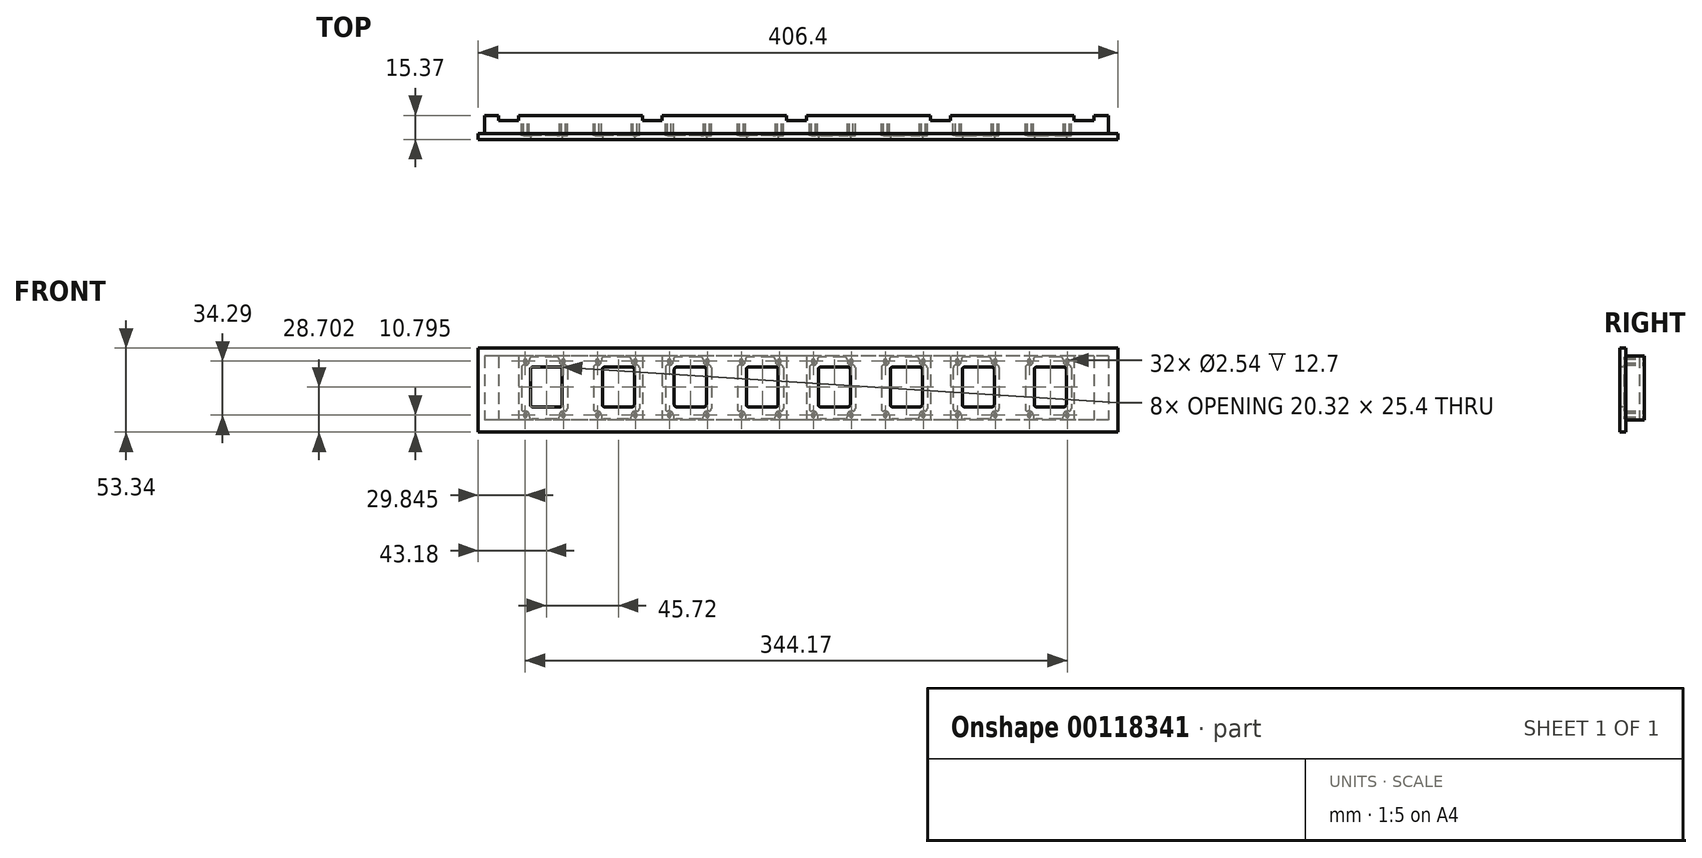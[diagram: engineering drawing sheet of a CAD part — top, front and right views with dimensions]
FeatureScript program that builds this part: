
annotation { "Feature Type Name" : "Feature", "Feature Type Description" : "" }
export const myFeature = defineFeature(function(context is Context, id is Id, definition is map)
    precondition{}
    {
        {
            var Q0;
            Q0=qCreatedBy(makeId("Front.planeOp"),FACE);
            var sketch = newSketch(context, id + "F0", { "sketchPlane" : qUnion([Q0])});
            skLineSegment(sketch, "E0.bottom", {"start": v(203.2, 26.67) * mm, "end": v(-203.2, 26.67) * mm});
            skLineSegment(sketch, "E0.top", {"start": v(203.2, -26.67) * mm, "end": v(-203.2, -26.67) * mm});
            skLineSegment(sketch, "E0.left", {"start": v(203.2, 26.67) * mm, "end": v(203.2, -26.67) * mm});
            skLineSegment(sketch, "E0.right", {"start": v(-203.2, 26.67) * mm, "end": v(-203.2, -26.67) * mm});
            skPoint(sketch, "E0.middle", {"position": v(0, 0) * mm});
            skSolve(sketch);
        }
        {
            var Q0;
            Q0 = qSketchRegion(id + "F0", true);
            extrude(context, id + "F1", {"entities" : qUnion([Q0]), "depth" : 3.8 * mm});
        }
        {
            var Q0;
            Q0=makeQuery(id+"F1.opExtrude","CAP_FACE",FACE,{"disambiguationData":[OSD([sQuery(id+"F0.wireOp",EDGE,"E0.bottom"),sQuery(id+"F0.wireOp",EDGE,"E0.top"),sQuery(id+"F0.wireOp",EDGE,"E0.left"),sQuery(id+"F0.wireOp",EDGE,"E0.right")])],"isStart":true});
            var sketch = newSketch(context, id + "F2", { "sketchPlane" : qUnion([Q0])});
            skLineSegment(sketch, "E1.bottom", {"start": v(-196.85, 21.59) * mm, "end": v(199.4, 21.59) * mm});
            skLineSegment(sketch, "E1.top", {"start": v(-196.85, -19.05) * mm, "end": v(199.4, -19.05) * mm});
            skLineSegment(sketch, "E1.left", {"start": v(-196.85, 21.59) * mm, "end": v(-196.85, -19.05) * mm});
            skLineSegment(sketch, "E1.right", {"start": v(199.4, 21.59) * mm, "end": v(199.4, -19.05) * mm});
            skSolve(sketch);
        }
        {
            var Q0;
            Q0 = qSketchRegion(id + "F2", true);
            extrude(context, id + "F3", {"entities" : qUnion([Q0]), "operationType" : NewBodyOperationType.ADD, "depth" : 11.56 * mm});
        }
        {
            var Q0;
            Q0=makeQuery(id+"F3.opExtrude","CAP_FACE",FACE,{"disambiguationData":[OSD([sQuery(id+"F2.wireOp",EDGE,"E1.bottom"),sQuery(id+"F2.wireOp",EDGE,"E1.top"),sQuery(id+"F2.wireOp",EDGE,"E1.left"),sQuery(id+"F2.wireOp",EDGE,"E1.right")])],"isStart":false});
            var sketch = newSketch(context, id + "F4", { "sketchPlane" : qUnion([Q0])});
            skLineSegment(sketch, "E2.bottom", {"start": v(-5.08, 21.59) * mm, "end": v(7.62, 21.59) * mm});
            skLineSegment(sketch, "E2.top", {"start": v(-5.08, -19.05) * mm, "end": v(7.62, -19.05) * mm});
            skLineSegment(sketch, "E2.left", {"start": v(-5.08, 21.59) * mm, "end": v(-5.08, -19.05) * mm});
            skLineSegment(sketch, "E2.right", {"start": v(7.62, 21.59) * mm, "end": v(7.62, -19.05) * mm});
            skLineSegment(sketch, "E3.1.0.0", {"start": v(86.36, -19.05) * mm, "end": v(99.06, -19.05) * mm});
            skLineSegment(sketch, "E3.1.0.1", {"start": v(86.36, 21.59) * mm, "end": v(99.06, 21.59) * mm});
            skLineSegment(sketch, "E3.1.0.2", {"start": v(86.36, 21.59) * mm, "end": v(86.36, -19.05) * mm});
            skLineSegment(sketch, "E3.1.0.3", {"start": v(99.06, 21.59) * mm, "end": v(99.06, -19.05) * mm});
            skLineSegment(sketch, "E3.2.0.0", {"start": v(177.8, -19.05) * mm, "end": v(190.5, -19.05) * mm});
            skLineSegment(sketch, "E3.2.0.1", {"start": v(177.8, 21.59) * mm, "end": v(190.5, 21.59) * mm});
            skLineSegment(sketch, "E3.2.0.2", {"start": v(177.8, 21.59) * mm, "end": v(177.8, -19.05) * mm});
            skLineSegment(sketch, "E3.2.0.3", {"start": v(190.5, 21.59) * mm, "end": v(190.5, -19.05) * mm});
            skLineSegment(sketch, "E3.direction1", {"start": v(-5.08, -19.05) * mm, "end": v(86.36, -19.05) * mm, "construction": true});
            skLineSegment(sketch, "E4.1.0.0", {"start": v(-96.52, 21.59) * mm, "end": v(-96.52, -19.05) * mm});
            skLineSegment(sketch, "E4.1.0.1", {"start": v(-96.52, -19.05) * mm, "end": v(-83.82, -19.05) * mm});
            skLineSegment(sketch, "E4.1.0.2", {"start": v(-96.52, 21.59) * mm, "end": v(-83.82, 21.59) * mm});
            skLineSegment(sketch, "E4.1.0.3", {"start": v(-83.82, 21.59) * mm, "end": v(-83.82, -19.05) * mm});
            skLineSegment(sketch, "E4.2.0.0", {"start": v(-187.96, 21.59) * mm, "end": v(-187.96, -19.05) * mm});
            skLineSegment(sketch, "E4.2.0.1", {"start": v(-187.96, -19.05) * mm, "end": v(-175.26, -19.05) * mm});
            skLineSegment(sketch, "E4.2.0.2", {"start": v(-187.96, 21.59) * mm, "end": v(-175.26, 21.59) * mm});
            skLineSegment(sketch, "E4.2.0.3", {"start": v(-175.26, 21.59) * mm, "end": v(-175.26, -19.05) * mm});
            skLineSegment(sketch, "E4.direction1", {"start": v(-5.08, -19.05) * mm, "end": v(-96.52, -19.05) * mm, "construction": true});
            skSolve(sketch);
        }
        {
            var Q0;
            Q0 = qSketchRegion(id + "F4", true);
            extrude(context, id + "F5", {"entities" : qUnion([Q0]), "operationType" : NewBodyOperationType.REMOVE, "oppositeDirection" : true, "depth" : 3.17 * mm});
        }
        {
            var Q0;
            {var subQ0=sQuery(id+"F2.wireOp",EDGE,"E1.bottom");var subQ1=sQuery(id+"F2.wireOp",EDGE,"E1.top");Q0=makeQuery(id+"F5.boolean.opBoolean","SPLIT",FACE,{"disambiguationData":[TD([makeQuery(id+"F5.opExtrude","SWEPT_FACE",FACE,{"disambiguationData":[OSD([sQuery(id+"F4.wireOp",EDGE,"E2.left")])]})])],"derivedFrom":makeQuery(id+"F3.opExtrude","CAP_FACE",FACE,{"disambiguationData":[OSD([subQ0,subQ1,sQuery(id+"F2.wireOp",EDGE,"E1.left"),sQuery(id+"F2.wireOp",EDGE,"E1.right")])],"isStart":false})});}
            var sketch = newSketch(context, id + "F6", { "sketchPlane" : qUnion([Q0])});
            skLineSegment(sketch, "E5.bottom", {"start": v(-174, 21.59) * mm, "end": v(-143.51, 21.59) * mm, "construction": true});
            skLineSegment(sketch, "E5.top", {"start": v(-174, -19.05) * mm, "end": v(-143.51, -19.05) * mm, "construction": true});
            skLineSegment(sketch, "E5.left", {"start": v(-174, 21.59) * mm, "end": v(-174, -19.05) * mm, "construction": true});
            skLineSegment(sketch, "E5.right", {"start": v(-143.51, 21.59) * mm, "end": v(-143.51, -19.05) * mm, "construction": true});
            skCircle(sketch, "E6", {"center": v(-170.82, 18.41) * mm, "radius": 1.27 * mm});
            skCircle(sketch, "E7", {"center": v(-146.69, 18.41) * mm, "radius": 1.27 * mm});
            skCircle(sketch, "E8", {"center": v(-146.69, -15.88) * mm, "radius": 1.27 * mm});
            skCircle(sketch, "E9", {"center": v(-170.82, -15.88) * mm, "radius": 1.27 * mm});
            skArc(sketch, "E10", {"start": v(-170.82, 15.87) * mm, "mid": v(-169.02, 16.62) * mm, "end": v(-168.28, 18.41) * mm});
            skArc(sketch, "E11", {"start": v(-149.23, 18.41) * mm, "mid": v(-148.48, 16.62) * mm, "end": v(-146.69, 15.87) * mm});
            skArc(sketch, "E12", {"start": v(-168.28, -15.88) * mm, "mid": v(-169.02, -14.08) * mm, "end": v(-170.82, -13.34) * mm});
            skArc(sketch, "E13", {"start": v(-146.69, -13.34) * mm, "mid": v(-148.48, -14.08) * mm, "end": v(-149.23, -15.88) * mm});
            skLineSegment(sketch, "E14.top", {"start": v(-168.28, -18.42) * mm, "end": v(-149.23, -18.42) * mm});
            skLineSegment(sketch, "E14.left", {"start": v(-173.36, 15.87) * mm, "end": v(-173.36, -13.34) * mm});
            skLineSegment(sketch, "E14.right", {"start": v(-144.15, 15.87) * mm, "end": v(-144.15, -13.33) * mm});
            skLineSegment(sketch, "E15", {"start": v(-173.36, 15.87) * mm, "end": v(-170.82, 15.87) * mm});
            skLineSegment(sketch, "E16", {"start": v(-173.36, -13.34) * mm, "end": v(-170.82, -13.34) * mm});
            skLineSegment(sketch, "E17", {"start": v(-168.28, 20.95) * mm, "end": v(-168.28, 18.41) * mm});
            skLineSegment(sketch, "E18", {"start": v(-149.23, 20.95) * mm, "end": v(-149.23, 18.41) * mm});
            skLineSegment(sketch, "E19.trimOffspring", {"start": v(-168.28, 20.95) * mm, "end": v(-149.23, 20.95) * mm});
            skLineSegment(sketch, "E20.trimOffspring", {"start": v(-168.28, -15.88) * mm, "end": v(-168.28, -18.42) * mm});
            skLineSegment(sketch, "E21.trimOffspring", {"start": v(-146.69, 15.87) * mm, "end": v(-144.15, 15.87) * mm});
            skLineSegment(sketch, "E22.trimOffspring", {"start": v(-149.23, -15.88) * mm, "end": v(-149.23, -18.42) * mm});
            skLineSegment(sketch, "E23.trimOffspring", {"start": v(-146.69, -13.33) * mm, "end": v(-144.15, -13.33) * mm});
            skLineSegment(sketch, "E24.bottom", {"start": v(-169.17, 14.6) * mm, "end": v(-148.85, 14.6) * mm, "construction": true});
            skLineSegment(sketch, "E24.top", {"start": v(-169.17, -13.33) * mm, "end": v(-148.85, -13.33) * mm, "construction": true});
            skLineSegment(sketch, "E24.left", {"start": v(-169.17, 14.6) * mm, "end": v(-169.17, -13.33) * mm, "construction": true});
            skLineSegment(sketch, "E24.right", {"start": v(-148.85, 14.6) * mm, "end": v(-148.85, -13.33) * mm, "construction": true});
            skLineSegment(sketch, "E25.1.0.0", {"start": v(-128.27, -19.05) * mm, "end": v(-97.8, -19.05) * mm, "construction": true});
            skLineSegment(sketch, "E25.1.0.1", {"start": v(-97.8, 21.59) * mm, "end": v(-97.8, -19.05) * mm, "construction": true});
            skLineSegment(sketch, "E25.1.0.2", {"start": v(-128.27, 21.59) * mm, "end": v(-128.27, -19.05) * mm, "construction": true});
            skLineSegment(sketch, "E25.1.0.3", {"start": v(-123.45, 14.6) * mm, "end": v(-123.45, -13.33) * mm, "construction": true});
            skLineSegment(sketch, "E25.1.0.4", {"start": v(-103.13, 14.6) * mm, "end": v(-103.13, -13.33) * mm, "construction": true});
            skLineSegment(sketch, "E25.1.0.5", {"start": v(-123.45, -13.33) * mm, "end": v(-103.13, -13.33) * mm, "construction": true});
            skLineSegment(sketch, "E25.1.0.6", {"start": v(-123.45, 14.6) * mm, "end": v(-103.13, 14.6) * mm, "construction": true});
            skLineSegment(sketch, "E25.1.0.7", {"start": v(-128.27, 21.59) * mm, "end": v(-97.8, 21.59) * mm, "construction": true});
            skLineSegment(sketch, "E25.1.0.8", {"start": v(-98.43, 15.87) * mm, "end": v(-98.43, -13.33) * mm});
            skLineSegment(sketch, "E25.1.0.9", {"start": v(-122.56, 20.95) * mm, "end": v(-103.5, 20.95) * mm});
            skLineSegment(sketch, "E25.1.0.10", {"start": v(-122.55, -18.42) * mm, "end": v(-103.5, -18.42) * mm});
            skLineSegment(sketch, "E25.1.0.11", {"start": v(-127.64, 15.87) * mm, "end": v(-127.64, -13.34) * mm});
            skCircle(sketch, "E25.1.0.12", {"center": v(-125.1, 18.41) * mm, "radius": 1.27 * mm});
            skCircle(sketch, "E25.1.0.13", {"center": v(-125.1, -15.88) * mm, "radius": 1.27 * mm});
            skLineSegment(sketch, "E25.1.0.14", {"start": v(-122.55, -15.88) * mm, "end": v(-122.55, -18.42) * mm});
            skLineSegment(sketch, "E25.1.0.15", {"start": v(-122.55, 20.95) * mm, "end": v(-122.55, 18.41) * mm});
            skCircle(sketch, "E25.1.0.16", {"center": v(-100.97, 18.41) * mm, "radius": 1.27 * mm});
            skLineSegment(sketch, "E25.1.0.17", {"start": v(-127.64, -13.33) * mm, "end": v(-125.1, -13.33) * mm});
            skLineSegment(sketch, "E25.1.0.18", {"start": v(-103.5, 20.95) * mm, "end": v(-103.5, 18.41) * mm});
            skArc(sketch, "E25.1.0.19", {"start": v(-122.56, -15.88) * mm, "mid": v(-123.3, -14.08) * mm, "end": v(-125.1, -13.34) * mm});
            skArc(sketch, "E25.1.0.20", {"start": v(-103.5, 18.41) * mm, "mid": v(-102.76, 16.62) * mm, "end": v(-100.97, 15.87) * mm});
            skArc(sketch, "E25.1.0.21", {"start": v(-125.1, 15.87) * mm, "mid": v(-123.3, 16.62) * mm, "end": v(-122.56, 18.41) * mm});
            skLineSegment(sketch, "E25.1.0.22", {"start": v(-103.5, -15.88) * mm, "end": v(-103.5, -18.42) * mm});
            skLineSegment(sketch, "E25.1.0.23", {"start": v(-127.64, 15.88) * mm, "end": v(-125.1, 15.88) * mm});
            skCircle(sketch, "E25.1.0.24", {"center": v(-100.97, -15.88) * mm, "radius": 1.27 * mm});
            skLineSegment(sketch, "E25.1.0.25", {"start": v(-100.97, 15.87) * mm, "end": v(-98.43, 15.87) * mm});
            skArc(sketch, "E25.1.0.26", {"start": v(-100.97, -13.34) * mm, "mid": v(-102.76, -14.08) * mm, "end": v(-103.5, -15.88) * mm});
            skLineSegment(sketch, "E25.1.0.27", {"start": v(-100.97, -13.33) * mm, "end": v(-98.43, -13.33) * mm});
            skLineSegment(sketch, "E25.2.0.0", {"start": v(-82.55, -19.05) * mm, "end": v(-52.07, -19.05) * mm, "construction": true});
            skLineSegment(sketch, "E25.2.0.1", {"start": v(-52.07, 21.59) * mm, "end": v(-52.07, -19.05) * mm, "construction": true});
            skLineSegment(sketch, "E25.2.0.2", {"start": v(-82.55, 21.59) * mm, "end": v(-82.55, -19.05) * mm, "construction": true});
            skLineSegment(sketch, "E25.2.0.3", {"start": v(-77.73, 14.6) * mm, "end": v(-77.73, -13.33) * mm, "construction": true});
            skLineSegment(sketch, "E25.2.0.4", {"start": v(-57.41, 14.6) * mm, "end": v(-57.41, -13.33) * mm, "construction": true});
            skLineSegment(sketch, "E25.2.0.5", {"start": v(-77.73, -13.33) * mm, "end": v(-57.41, -13.33) * mm, "construction": true});
            skLineSegment(sketch, "E25.2.0.6", {"start": v(-77.73, 14.6) * mm, "end": v(-57.41, 14.6) * mm, "construction": true});
            skLineSegment(sketch, "E25.2.0.7", {"start": v(-82.55, 21.59) * mm, "end": v(-52.07, 21.59) * mm, "construction": true});
            skLineSegment(sketch, "E25.2.0.8", {"start": v(-52.7, 15.87) * mm, "end": v(-52.7, -13.33) * mm});
            skLineSegment(sketch, "E25.2.0.9", {"start": v(-76.84, 20.95) * mm, "end": v(-57.79, 20.95) * mm});
            skLineSegment(sketch, "E25.2.0.10", {"start": v(-76.83, -18.42) * mm, "end": v(-57.79, -18.42) * mm});
            skLineSegment(sketch, "E25.2.0.11", {"start": v(-81.91, 15.87) * mm, "end": v(-81.91, -13.34) * mm});
            skCircle(sketch, "E25.2.0.12", {"center": v(-79.38, 18.41) * mm, "radius": 1.27 * mm});
            skCircle(sketch, "E25.2.0.13", {"center": v(-79.38, -15.88) * mm, "radius": 1.27 * mm});
            skLineSegment(sketch, "E25.2.0.14", {"start": v(-76.83, -15.88) * mm, "end": v(-76.83, -18.42) * mm});
            skLineSegment(sketch, "E25.2.0.15", {"start": v(-76.83, 20.95) * mm, "end": v(-76.83, 18.41) * mm});
            skCircle(sketch, "E25.2.0.16", {"center": v(-55.25, 18.41) * mm, "radius": 1.27 * mm});
            skLineSegment(sketch, "E25.2.0.17", {"start": v(-81.91, -13.33) * mm, "end": v(-79.38, -13.33) * mm});
            skLineSegment(sketch, "E25.2.0.18", {"start": v(-57.79, 20.95) * mm, "end": v(-57.79, 18.41) * mm});
            skArc(sketch, "E25.2.0.19", {"start": v(-76.83, -15.88) * mm, "mid": v(-77.58, -14.08) * mm, "end": v(-79.38, -13.34) * mm});
            skArc(sketch, "E25.2.0.20", {"start": v(-57.79, 18.41) * mm, "mid": v(-57.04, 16.62) * mm, "end": v(-55.25, 15.87) * mm});
            skArc(sketch, "E25.2.0.21", {"start": v(-79.38, 15.87) * mm, "mid": v(-77.58, 16.62) * mm, "end": v(-76.83, 18.41) * mm});
            skLineSegment(sketch, "E25.2.0.22", {"start": v(-57.79, -15.88) * mm, "end": v(-57.79, -18.42) * mm});
            skLineSegment(sketch, "E25.2.0.23", {"start": v(-81.91, 15.88) * mm, "end": v(-79.38, 15.88) * mm});
            skCircle(sketch, "E25.2.0.24", {"center": v(-55.25, -15.88) * mm, "radius": 1.27 * mm});
            skLineSegment(sketch, "E25.2.0.25", {"start": v(-55.25, 15.87) * mm, "end": v(-52.7, 15.87) * mm});
            skArc(sketch, "E25.2.0.26", {"start": v(-55.25, -13.34) * mm, "mid": v(-57.04, -14.08) * mm, "end": v(-57.79, -15.88) * mm});
            skLineSegment(sketch, "E25.2.0.27", {"start": v(-55.25, -13.33) * mm, "end": v(-52.7, -13.33) * mm});
            skLineSegment(sketch, "E25.3.0.0", {"start": v(-36.83, -19.05) * mm, "end": v(-6.35, -19.05) * mm, "construction": true});
            skLineSegment(sketch, "E25.3.0.1", {"start": v(-6.35, 21.59) * mm, "end": v(-6.35, -19.05) * mm, "construction": true});
            skLineSegment(sketch, "E25.3.0.2", {"start": v(-36.83, 21.59) * mm, "end": v(-36.83, -19.05) * mm, "construction": true});
            skLineSegment(sketch, "E25.3.0.3", {"start": v(-32.01, 14.6) * mm, "end": v(-32.01, -13.33) * mm, "construction": true});
            skLineSegment(sketch, "E25.3.0.4", {"start": v(-11.7, 14.6) * mm, "end": v(-11.7, -13.33) * mm, "construction": true});
            skLineSegment(sketch, "E25.3.0.5", {"start": v(-32.01, -13.33) * mm, "end": v(-11.7, -13.33) * mm, "construction": true});
            skLineSegment(sketch, "E25.3.0.6", {"start": v(-32.01, 14.6) * mm, "end": v(-11.7, 14.6) * mm, "construction": true});
            skLineSegment(sketch, "E25.3.0.7", {"start": v(-36.83, 21.59) * mm, "end": v(-6.35, 21.59) * mm, "construction": true});
            skLineSegment(sketch, "E25.3.0.8", {"start": v(-6.98, 15.87) * mm, "end": v(-6.98, -13.33) * mm});
            skLineSegment(sketch, "E25.3.0.9", {"start": v(-31.12, 20.95) * mm, "end": v(-12.07, 20.95) * mm});
            skLineSegment(sketch, "E25.3.0.10", {"start": v(-31.11, -18.42) * mm, "end": v(-12.07, -18.42) * mm});
            skLineSegment(sketch, "E25.3.0.11", {"start": v(-36.2, 15.87) * mm, "end": v(-36.2, -13.34) * mm});
            skCircle(sketch, "E25.3.0.12", {"center": v(-33.65, 18.41) * mm, "radius": 1.27 * mm});
            skCircle(sketch, "E25.3.0.13", {"center": v(-33.65, -15.88) * mm, "radius": 1.27 * mm});
            skLineSegment(sketch, "E25.3.0.14", {"start": v(-31.11, -15.88) * mm, "end": v(-31.11, -18.42) * mm});
            skLineSegment(sketch, "E25.3.0.15", {"start": v(-31.11, 20.95) * mm, "end": v(-31.11, 18.41) * mm});
            skCircle(sketch, "E25.3.0.16", {"center": v(-9.53, 18.41) * mm, "radius": 1.27 * mm});
            skLineSegment(sketch, "E25.3.0.17", {"start": v(-36.2, -13.33) * mm, "end": v(-33.65, -13.33) * mm});
            skLineSegment(sketch, "E25.3.0.18", {"start": v(-12.07, 20.95) * mm, "end": v(-12.07, 18.41) * mm});
            skArc(sketch, "E25.3.0.19", {"start": v(-31.11, -15.88) * mm, "mid": v(-31.86, -14.08) * mm, "end": v(-33.65, -13.34) * mm});
            skArc(sketch, "E25.3.0.20", {"start": v(-12.07, 18.41) * mm, "mid": v(-11.32, 16.62) * mm, "end": v(-9.53, 15.87) * mm});
            skArc(sketch, "E25.3.0.21", {"start": v(-33.65, 15.87) * mm, "mid": v(-31.86, 16.62) * mm, "end": v(-31.11, 18.41) * mm});
            skLineSegment(sketch, "E25.3.0.22", {"start": v(-12.07, -15.88) * mm, "end": v(-12.07, -18.42) * mm});
            skLineSegment(sketch, "E25.3.0.23", {"start": v(-36.2, 15.88) * mm, "end": v(-33.65, 15.88) * mm});
            skCircle(sketch, "E25.3.0.24", {"center": v(-9.53, -15.88) * mm, "radius": 1.27 * mm});
            skLineSegment(sketch, "E25.3.0.25", {"start": v(-9.53, 15.87) * mm, "end": v(-6.98, 15.87) * mm});
            skArc(sketch, "E25.3.0.26", {"start": v(-9.53, -13.34) * mm, "mid": v(-11.32, -14.08) * mm, "end": v(-12.07, -15.88) * mm});
            skLineSegment(sketch, "E25.3.0.27", {"start": v(-9.53, -13.33) * mm, "end": v(-6.98, -13.33) * mm});
            skLineSegment(sketch, "E25.4.0.0", {"start": v(8.9, -19.05) * mm, "end": v(39.37, -19.05) * mm, "construction": true});
            skLineSegment(sketch, "E25.4.0.1", {"start": v(39.37, 21.59) * mm, "end": v(39.37, -19.05) * mm, "construction": true});
            skLineSegment(sketch, "E25.4.0.2", {"start": v(8.9, 21.59) * mm, "end": v(8.9, -19.05) * mm, "construction": true});
            skLineSegment(sketch, "E25.4.0.3", {"start": v(13.7, 14.6) * mm, "end": v(13.7, -13.33) * mm, "construction": true});
            skLineSegment(sketch, "E25.4.0.4", {"start": v(34.03, 14.6) * mm, "end": v(34.03, -13.33) * mm, "construction": true});
            skLineSegment(sketch, "E25.4.0.5", {"start": v(13.7, -13.33) * mm, "end": v(34.03, -13.33) * mm, "construction": true});
            skLineSegment(sketch, "E25.4.0.6", {"start": v(13.7, 14.6) * mm, "end": v(34.03, 14.6) * mm, "construction": true});
            skLineSegment(sketch, "E25.4.0.7", {"start": v(8.9, 21.59) * mm, "end": v(39.37, 21.59) * mm, "construction": true});
            skLineSegment(sketch, "E25.4.0.8", {"start": v(38.74, 15.87) * mm, "end": v(38.74, -13.33) * mm});
            skLineSegment(sketch, "E25.4.0.9", {"start": v(14.6, 20.95) * mm, "end": v(33.65, 20.95) * mm});
            skLineSegment(sketch, "E25.4.0.10", {"start": v(14.6, -18.42) * mm, "end": v(33.65, -18.42) * mm});
            skLineSegment(sketch, "E25.4.0.11", {"start": v(9.53, 15.87) * mm, "end": v(9.53, -13.34) * mm});
            skCircle(sketch, "E25.4.0.12", {"center": v(12.07, 18.41) * mm, "radius": 1.27 * mm});
            skCircle(sketch, "E25.4.0.13", {"center": v(12.07, -15.88) * mm, "radius": 1.27 * mm});
            skLineSegment(sketch, "E25.4.0.14", {"start": v(14.6, -15.88) * mm, "end": v(14.6, -18.42) * mm});
            skLineSegment(sketch, "E25.4.0.15", {"start": v(14.6, 20.95) * mm, "end": v(14.6, 18.41) * mm});
            skCircle(sketch, "E25.4.0.16", {"center": v(36.2, 18.41) * mm, "radius": 1.27 * mm});
            skLineSegment(sketch, "E25.4.0.17", {"start": v(9.53, -13.33) * mm, "end": v(12.07, -13.33) * mm});
            skLineSegment(sketch, "E25.4.0.18", {"start": v(33.65, 20.95) * mm, "end": v(33.65, 18.41) * mm});
            skArc(sketch, "E25.4.0.19", {"start": v(14.6, -15.88) * mm, "mid": v(13.86, -14.08) * mm, "end": v(12.07, -13.34) * mm});
            skArc(sketch, "E25.4.0.20", {"start": v(33.66, 18.41) * mm, "mid": v(34.4, 16.62) * mm, "end": v(36.2, 15.87) * mm});
            skArc(sketch, "E25.4.0.21", {"start": v(12.07, 15.87) * mm, "mid": v(13.86, 16.62) * mm, "end": v(14.6, 18.41) * mm});
            skLineSegment(sketch, "E25.4.0.22", {"start": v(33.65, -15.88) * mm, "end": v(33.65, -18.42) * mm});
            skLineSegment(sketch, "E25.4.0.23", {"start": v(9.53, 15.88) * mm, "end": v(12.07, 15.88) * mm});
            skCircle(sketch, "E25.4.0.24", {"center": v(36.2, -15.88) * mm, "radius": 1.27 * mm});
            skLineSegment(sketch, "E25.4.0.25", {"start": v(36.2, 15.87) * mm, "end": v(38.74, 15.87) * mm});
            skArc(sketch, "E25.4.0.26", {"start": v(36.2, -13.34) * mm, "mid": v(34.4, -14.08) * mm, "end": v(33.66, -15.88) * mm});
            skLineSegment(sketch, "E25.4.0.27", {"start": v(36.2, -13.33) * mm, "end": v(38.74, -13.33) * mm});
            skLineSegment(sketch, "E25.5.0.0", {"start": v(54.61, -19.05) * mm, "end": v(85.1, -19.05) * mm, "construction": true});
            skLineSegment(sketch, "E25.5.0.1", {"start": v(85.1, 21.59) * mm, "end": v(85.1, -19.05) * mm, "construction": true});
            skLineSegment(sketch, "E25.5.0.2", {"start": v(54.61, 21.59) * mm, "end": v(54.61, -19.05) * mm, "construction": true});
            skLineSegment(sketch, "E25.5.0.3", {"start": v(59.43, 14.6) * mm, "end": v(59.43, -13.33) * mm, "construction": true});
            skLineSegment(sketch, "E25.5.0.4", {"start": v(79.75, 14.6) * mm, "end": v(79.75, -13.33) * mm, "construction": true});
            skLineSegment(sketch, "E25.5.0.5", {"start": v(59.43, -13.33) * mm, "end": v(79.75, -13.33) * mm, "construction": true});
            skLineSegment(sketch, "E25.5.0.6", {"start": v(59.43, 14.6) * mm, "end": v(79.75, 14.6) * mm, "construction": true});
            skLineSegment(sketch, "E25.5.0.7", {"start": v(54.61, 21.59) * mm, "end": v(85.1, 21.59) * mm, "construction": true});
            skLineSegment(sketch, "E25.5.0.8", {"start": v(84.46, 15.87) * mm, "end": v(84.46, -13.33) * mm});
            skLineSegment(sketch, "E25.5.0.9", {"start": v(60.33, 20.95) * mm, "end": v(79.38, 20.95) * mm});
            skLineSegment(sketch, "E25.5.0.10", {"start": v(60.33, -18.42) * mm, "end": v(79.38, -18.42) * mm});
            skLineSegment(sketch, "E25.5.0.11", {"start": v(55.25, 15.87) * mm, "end": v(55.25, -13.34) * mm});
            skCircle(sketch, "E25.5.0.12", {"center": v(57.79, 18.41) * mm, "radius": 1.27 * mm});
            skCircle(sketch, "E25.5.0.13", {"center": v(57.79, -15.88) * mm, "radius": 1.27 * mm});
            skLineSegment(sketch, "E25.5.0.14", {"start": v(60.33, -15.88) * mm, "end": v(60.33, -18.42) * mm});
            skLineSegment(sketch, "E25.5.0.15", {"start": v(60.33, 20.95) * mm, "end": v(60.33, 18.41) * mm});
            skCircle(sketch, "E25.5.0.16", {"center": v(81.92, 18.41) * mm, "radius": 1.27 * mm});
            skLineSegment(sketch, "E25.5.0.17", {"start": v(55.25, -13.33) * mm, "end": v(57.79, -13.33) * mm});
            skLineSegment(sketch, "E25.5.0.18", {"start": v(79.38, 20.95) * mm, "end": v(79.38, 18.41) * mm});
            skArc(sketch, "E25.5.0.19", {"start": v(60.33, -15.88) * mm, "mid": v(59.58, -14.08) * mm, "end": v(57.79, -13.34) * mm});
            skArc(sketch, "E25.5.0.20", {"start": v(79.38, 18.41) * mm, "mid": v(80.12, 16.62) * mm, "end": v(81.92, 15.87) * mm});
            skArc(sketch, "E25.5.0.21", {"start": v(57.79, 15.87) * mm, "mid": v(59.58, 16.62) * mm, "end": v(60.33, 18.41) * mm});
            skLineSegment(sketch, "E25.5.0.22", {"start": v(79.38, -15.88) * mm, "end": v(79.38, -18.42) * mm});
            skLineSegment(sketch, "E25.5.0.23", {"start": v(55.25, 15.88) * mm, "end": v(57.79, 15.88) * mm});
            skCircle(sketch, "E25.5.0.24", {"center": v(81.92, -15.88) * mm, "radius": 1.27 * mm});
            skLineSegment(sketch, "E25.5.0.25", {"start": v(81.92, 15.87) * mm, "end": v(84.46, 15.87) * mm});
            skArc(sketch, "E25.5.0.26", {"start": v(81.92, -13.34) * mm, "mid": v(80.12, -14.08) * mm, "end": v(79.38, -15.88) * mm});
            skLineSegment(sketch, "E25.5.0.27", {"start": v(81.92, -13.33) * mm, "end": v(84.46, -13.33) * mm});
            skLineSegment(sketch, "E25.6.0.0", {"start": v(100.33, -19.05) * mm, "end": v(130.81, -19.05) * mm, "construction": true});
            skLineSegment(sketch, "E25.6.0.1", {"start": v(130.81, 21.59) * mm, "end": v(130.81, -19.05) * mm, "construction": true});
            skLineSegment(sketch, "E25.6.0.2", {"start": v(100.33, 21.59) * mm, "end": v(100.33, -19.05) * mm, "construction": true});
            skLineSegment(sketch, "E25.6.0.3", {"start": v(105.15, 14.6) * mm, "end": v(105.15, -13.33) * mm, "construction": true});
            skLineSegment(sketch, "E25.6.0.4", {"start": v(125.47, 14.6) * mm, "end": v(125.47, -13.33) * mm, "construction": true});
            skLineSegment(sketch, "E25.6.0.5", {"start": v(105.15, -13.33) * mm, "end": v(125.47, -13.33) * mm, "construction": true});
            skLineSegment(sketch, "E25.6.0.6", {"start": v(105.15, 14.6) * mm, "end": v(125.47, 14.6) * mm, "construction": true});
            skLineSegment(sketch, "E25.6.0.7", {"start": v(100.33, 21.59) * mm, "end": v(130.81, 21.59) * mm, "construction": true});
            skLineSegment(sketch, "E25.6.0.8", {"start": v(130.18, 15.87) * mm, "end": v(130.18, -13.33) * mm});
            skLineSegment(sketch, "E25.6.0.9", {"start": v(106.05, 20.95) * mm, "end": v(125.1, 20.95) * mm});
            skLineSegment(sketch, "E25.6.0.10", {"start": v(106.05, -18.42) * mm, "end": v(125.1, -18.42) * mm});
            skLineSegment(sketch, "E25.6.0.11", {"start": v(100.97, 15.87) * mm, "end": v(100.97, -13.34) * mm});
            skCircle(sketch, "E25.6.0.12", {"center": v(103.5, 18.41) * mm, "radius": 1.27 * mm});
            skCircle(sketch, "E25.6.0.13", {"center": v(103.5, -15.88) * mm, "radius": 1.27 * mm});
            skLineSegment(sketch, "E25.6.0.14", {"start": v(106.05, -15.88) * mm, "end": v(106.05, -18.42) * mm});
            skLineSegment(sketch, "E25.6.0.15", {"start": v(106.05, 20.95) * mm, "end": v(106.05, 18.41) * mm});
            skCircle(sketch, "E25.6.0.16", {"center": v(127.64, 18.41) * mm, "radius": 1.27 * mm});
            skLineSegment(sketch, "E25.6.0.17", {"start": v(100.97, -13.33) * mm, "end": v(103.5, -13.33) * mm});
            skLineSegment(sketch, "E25.6.0.18", {"start": v(125.1, 20.95) * mm, "end": v(125.1, 18.41) * mm});
            skArc(sketch, "E25.6.0.19", {"start": v(106.05, -15.88) * mm, "mid": v(105.3, -14.08) * mm, "end": v(103.5, -13.34) * mm});
            skArc(sketch, "E25.6.0.20", {"start": v(125.1, 18.41) * mm, "mid": v(125.84, 16.62) * mm, "end": v(127.64, 15.87) * mm});
            skArc(sketch, "E25.6.0.21", {"start": v(103.5, 15.87) * mm, "mid": v(105.3, 16.62) * mm, "end": v(106.05, 18.41) * mm});
            skLineSegment(sketch, "E25.6.0.22", {"start": v(125.1, -15.88) * mm, "end": v(125.1, -18.42) * mm});
            skLineSegment(sketch, "E25.6.0.23", {"start": v(100.97, 15.88) * mm, "end": v(103.5, 15.88) * mm});
            skCircle(sketch, "E25.6.0.24", {"center": v(127.64, -15.88) * mm, "radius": 1.27 * mm});
            skLineSegment(sketch, "E25.6.0.25", {"start": v(127.64, 15.87) * mm, "end": v(130.18, 15.87) * mm});
            skArc(sketch, "E25.6.0.26", {"start": v(127.64, -13.34) * mm, "mid": v(125.84, -14.08) * mm, "end": v(125.1, -15.88) * mm});
            skLineSegment(sketch, "E25.6.0.27", {"start": v(127.64, -13.33) * mm, "end": v(130.18, -13.33) * mm});
            skLineSegment(sketch, "E25.7.0.0", {"start": v(146.05, -19.05) * mm, "end": v(176.53, -19.05) * mm, "construction": true});
            skLineSegment(sketch, "E25.7.0.1", {"start": v(176.53, 21.59) * mm, "end": v(176.53, -19.05) * mm, "construction": true});
            skLineSegment(sketch, "E25.7.0.2", {"start": v(146.05, 21.59) * mm, "end": v(146.05, -19.05) * mm, "construction": true});
            skLineSegment(sketch, "E25.7.0.3", {"start": v(150.87, 14.6) * mm, "end": v(150.87, -13.33) * mm, "construction": true});
            skLineSegment(sketch, "E25.7.0.4", {"start": v(171.19, 14.6) * mm, "end": v(171.19, -13.33) * mm, "construction": true});
            skLineSegment(sketch, "E25.7.0.5", {"start": v(150.87, -13.33) * mm, "end": v(171.19, -13.33) * mm, "construction": true});
            skLineSegment(sketch, "E25.7.0.6", {"start": v(150.87, 14.6) * mm, "end": v(171.19, 14.6) * mm, "construction": true});
            skLineSegment(sketch, "E25.7.0.7", {"start": v(146.05, 21.59) * mm, "end": v(176.53, 21.59) * mm, "construction": true});
            skLineSegment(sketch, "E25.7.0.8", {"start": v(175.9, 15.87) * mm, "end": v(175.9, -13.33) * mm});
            skLineSegment(sketch, "E25.7.0.9", {"start": v(151.77, 20.95) * mm, "end": v(170.82, 20.95) * mm});
            skLineSegment(sketch, "E25.7.0.10", {"start": v(151.77, -18.42) * mm, "end": v(170.82, -18.42) * mm});
            skLineSegment(sketch, "E25.7.0.11", {"start": v(146.69, 15.87) * mm, "end": v(146.69, -13.34) * mm});
            skCircle(sketch, "E25.7.0.12", {"center": v(149.23, 18.41) * mm, "radius": 1.27 * mm});
            skCircle(sketch, "E25.7.0.13", {"center": v(149.23, -15.88) * mm, "radius": 1.27 * mm});
            skLineSegment(sketch, "E25.7.0.14", {"start": v(151.77, -15.88) * mm, "end": v(151.77, -18.42) * mm});
            skLineSegment(sketch, "E25.7.0.15", {"start": v(151.77, 20.95) * mm, "end": v(151.77, 18.41) * mm});
            skCircle(sketch, "E25.7.0.16", {"center": v(173.36, 18.41) * mm, "radius": 1.27 * mm});
            skLineSegment(sketch, "E25.7.0.17", {"start": v(146.69, -13.33) * mm, "end": v(149.23, -13.33) * mm});
            skLineSegment(sketch, "E25.7.0.18", {"start": v(170.82, 20.95) * mm, "end": v(170.82, 18.41) * mm});
            skArc(sketch, "E25.7.0.19", {"start": v(151.77, -15.88) * mm, "mid": v(151.02, -14.08) * mm, "end": v(149.23, -13.34) * mm});
            skArc(sketch, "E25.7.0.20", {"start": v(170.82, 18.41) * mm, "mid": v(171.56, 16.62) * mm, "end": v(173.36, 15.87) * mm});
            skArc(sketch, "E25.7.0.21", {"start": v(149.23, 15.87) * mm, "mid": v(151.02, 16.62) * mm, "end": v(151.77, 18.41) * mm});
            skLineSegment(sketch, "E25.7.0.22", {"start": v(170.82, -15.88) * mm, "end": v(170.82, -18.42) * mm});
            skLineSegment(sketch, "E25.7.0.23", {"start": v(146.69, 15.88) * mm, "end": v(149.23, 15.88) * mm});
            skCircle(sketch, "E25.7.0.24", {"center": v(173.36, -15.88) * mm, "radius": 1.27 * mm});
            skLineSegment(sketch, "E25.7.0.25", {"start": v(173.36, 15.87) * mm, "end": v(175.9, 15.87) * mm});
            skArc(sketch, "E25.7.0.26", {"start": v(173.36, -13.34) * mm, "mid": v(171.56, -14.08) * mm, "end": v(170.82, -15.88) * mm});
            skLineSegment(sketch, "E25.7.0.27", {"start": v(173.36, -13.33) * mm, "end": v(175.9, -13.33) * mm});
            skLineSegment(sketch, "E25.direction1", {"start": v(-174, -19.05) * mm, "end": v(-128.27, -19.05) * mm, "construction": true});
            skSolve(sketch);
        }
        {
            var Q0;
            Q0 = qSketchRegion(id + "F6", true);
            extrude(context, id + "F7", {"entities" : qUnion([Q0]), "operationType" : NewBodyOperationType.REMOVE, "oppositeDirection" : true, "depth" : 12.7 * mm});
        }
        {
            var Q0;
            Q0=makeQuery(id+"F1.opExtrude","CAP_FACE",FACE,{"disambiguationData":[OSD([sQuery(id+"F0.wireOp",EDGE,"E0.bottom"),sQuery(id+"F0.wireOp",EDGE,"E0.top"),sQuery(id+"F0.wireOp",EDGE,"E0.left"),sQuery(id+"F0.wireOp",EDGE,"E0.right")])],"isStart":false});
            var sketch = newSketch(context, id + "F8", { "sketchPlane" : qUnion([Q0])});
            skLineSegment(sketch, "E26.bottom", {"start": v(-33.02, 14.73) * mm, "end": v(-12.7, 14.73) * mm});
            skLineSegment(sketch, "E26.top", {"start": v(-33.02, -10.67) * mm, "end": v(-12.7, -10.67) * mm});
            skLineSegment(sketch, "E26.left", {"start": v(-33.02, 14.73) * mm, "end": v(-33.02, -10.67) * mm});
            skLineSegment(sketch, "E26.right", {"start": v(-12.7, 14.73) * mm, "end": v(-12.7, -10.67) * mm});
            skLineSegment(sketch, "E27.1.0.0", {"start": v(-58.42, 14.73) * mm, "end": v(-58.42, -10.67) * mm});
            skLineSegment(sketch, "E27.1.0.1", {"start": v(-78.74, 14.73) * mm, "end": v(-78.74, -10.67) * mm});
            skLineSegment(sketch, "E27.1.0.2", {"start": v(-78.74, -10.67) * mm, "end": v(-58.42, -10.67) * mm});
            skLineSegment(sketch, "E27.1.0.3", {"start": v(-78.74, 14.73) * mm, "end": v(-58.42, 14.73) * mm});
            skLineSegment(sketch, "E27.2.0.0", {"start": v(-104.14, 14.73) * mm, "end": v(-104.14, -10.67) * mm});
            skLineSegment(sketch, "E27.2.0.1", {"start": v(-124.46, 14.73) * mm, "end": v(-124.46, -10.67) * mm});
            skLineSegment(sketch, "E27.2.0.2", {"start": v(-124.46, -10.67) * mm, "end": v(-104.14, -10.67) * mm});
            skLineSegment(sketch, "E27.2.0.3", {"start": v(-124.46, 14.73) * mm, "end": v(-104.14, 14.73) * mm});
            skLineSegment(sketch, "E27.3.0.0", {"start": v(-149.86, 14.73) * mm, "end": v(-149.86, -10.67) * mm});
            skLineSegment(sketch, "E27.3.0.1", {"start": v(-170.18, 14.73) * mm, "end": v(-170.18, -10.67) * mm});
            skLineSegment(sketch, "E27.3.0.2", {"start": v(-170.18, -10.67) * mm, "end": v(-149.86, -10.67) * mm});
            skLineSegment(sketch, "E27.3.0.3", {"start": v(-170.18, 14.73) * mm, "end": v(-149.86, 14.73) * mm});
            skLineSegment(sketch, "E27.direction1", {"start": v(-33.02, -10.67) * mm, "end": v(-78.74, -10.67) * mm, "construction": true});
            skLineSegment(sketch, "E28.MirrorCS", {"start": v(78.74, -10.67) * mm, "end": v(58.42, -10.67) * mm});
            skLineSegment(sketch, "E29.MirrorCS", {"start": v(149.86, 14.73) * mm, "end": v(149.86, -10.67) * mm});
            skLineSegment(sketch, "E30.MirrorCS", {"start": v(124.46, 14.73) * mm, "end": v(104.14, 14.73) * mm});
            skLineSegment(sketch, "E31.MirrorCS", {"start": v(124.46, -10.67) * mm, "end": v(104.14, -10.67) * mm});
            skLineSegment(sketch, "E32.MirrorCS", {"start": v(33.02, 14.73) * mm, "end": v(12.7, 14.73) * mm});
            skLineSegment(sketch, "E33.MirrorCS", {"start": v(33.02, -10.67) * mm, "end": v(12.7, -10.67) * mm});
            skLineSegment(sketch, "E34.MirrorCS", {"start": v(33.02, 14.73) * mm, "end": v(33.02, -10.67) * mm});
            skLineSegment(sketch, "E35.MirrorCS", {"start": v(12.7, 14.73) * mm, "end": v(12.7, -10.67) * mm});
            skLineSegment(sketch, "E36.MirrorCS", {"start": v(58.42, 14.73) * mm, "end": v(58.42, -10.67) * mm});
            skLineSegment(sketch, "E37.MirrorCS", {"start": v(78.74, 14.73) * mm, "end": v(78.74, -10.67) * mm});
            skLineSegment(sketch, "E38.MirrorCS", {"start": v(78.74, 14.73) * mm, "end": v(58.42, 14.73) * mm});
            skLineSegment(sketch, "E39.MirrorCS", {"start": v(104.14, 14.73) * mm, "end": v(104.14, -10.67) * mm});
            skLineSegment(sketch, "E40.MirrorCS", {"start": v(170.18, -10.67) * mm, "end": v(149.86, -10.67) * mm});
            skLineSegment(sketch, "E41.MirrorCS", {"start": v(170.18, 14.73) * mm, "end": v(170.18, -10.67) * mm});
            skLineSegment(sketch, "E42.MirrorCS", {"start": v(170.18, 14.73) * mm, "end": v(149.86, 14.73) * mm});
            skLineSegment(sketch, "E43.MirrorCS", {"start": v(33.02, -10.67) * mm, "end": v(78.74, -10.67) * mm, "construction": true});
            skLineSegment(sketch, "E44.MirrorCS", {"start": v(124.46, 14.73) * mm, "end": v(124.46, -10.67) * mm});
            skSolve(sketch);
        }
        {
            var Q0;
            Q0 = qSketchRegion(id + "F8", true);
            extrude(context, id + "F9", {"entities" : qUnion([Q0]), "operationType" : NewBodyOperationType.REMOVE, "oppositeDirection" : true, "depth" : 25.4 * mm});
        }
        {
            var Q0;
            Q0=makeQuery(id+"F9.boolean.opBoolean","COPY",EDGE,{"derivedFrom":makeQuery(id+"F9.opExtrude","SWEPT_EDGE",EDGE,{"disambiguationData":[OSD([sQuery(id+"F8.wireOp",EDGE,"E27.3.0.1"),sQuery(id+"F8.wireOp",EDGE,"E27.3.0.2")])]})});
            var Q1;
            Q1=makeQuery(id+"F9.boolean.opBoolean","COPY",EDGE,{"derivedFrom":makeQuery(id+"F9.opExtrude","SWEPT_EDGE",EDGE,{"disambiguationData":[OSD([sQuery(id+"F8.wireOp",EDGE,"E27.3.0.0"),sQuery(id+"F8.wireOp",EDGE,"E27.3.0.2")])]})});
            var Q2;
            Q2=makeQuery(id+"F9.boolean.opBoolean","COPY",EDGE,{"derivedFrom":makeQuery(id+"F9.opExtrude","SWEPT_EDGE",EDGE,{"disambiguationData":[OSD([sQuery(id+"F8.wireOp",EDGE,"E27.3.0.1"),sQuery(id+"F8.wireOp",EDGE,"E27.3.0.3")])]})});
            var Q3;
            Q3=makeQuery(id+"F9.boolean.opBoolean","COPY",EDGE,{"derivedFrom":makeQuery(id+"F9.opExtrude","SWEPT_EDGE",EDGE,{"disambiguationData":[OSD([sQuery(id+"F8.wireOp",EDGE,"E27.3.0.0"),sQuery(id+"F8.wireOp",EDGE,"E27.3.0.3")])]})});
            var Q4;
            Q4=makeQuery(id+"F9.boolean.opBoolean","COPY",EDGE,{"derivedFrom":makeQuery(id+"F9.opExtrude","SWEPT_EDGE",EDGE,{"disambiguationData":[OSD([sQuery(id+"F8.wireOp",EDGE,"E27.2.0.0"),sQuery(id+"F8.wireOp",EDGE,"E27.2.0.3")])]})});
            var Q5;
            Q5=makeQuery(id+"F9.boolean.opBoolean","COPY",EDGE,{"derivedFrom":makeQuery(id+"F9.opExtrude","SWEPT_EDGE",EDGE,{"disambiguationData":[OSD([sQuery(id+"F8.wireOp",EDGE,"E27.2.0.0"),sQuery(id+"F8.wireOp",EDGE,"E27.2.0.2")])]})});
            var Q6;
            Q6=makeQuery(id+"F9.boolean.opBoolean","COPY",EDGE,{"derivedFrom":makeQuery(id+"F9.opExtrude","SWEPT_EDGE",EDGE,{"disambiguationData":[OSD([sQuery(id+"F8.wireOp",EDGE,"E27.1.0.0"),sQuery(id+"F8.wireOp",EDGE,"E27.1.0.2")])]})});
            var Q7;
            Q7=makeQuery(id+"F9.boolean.opBoolean","COPY",EDGE,{"derivedFrom":makeQuery(id+"F9.opExtrude","SWEPT_EDGE",EDGE,{"disambiguationData":[OSD([sQuery(id+"F8.wireOp",EDGE,"E27.1.0.0"),sQuery(id+"F8.wireOp",EDGE,"E27.1.0.3")])]})});
            var Q8;
            Q8=makeQuery(id+"F9.boolean.opBoolean","COPY",EDGE,{"derivedFrom":makeQuery(id+"F9.opExtrude","SWEPT_EDGE",EDGE,{"disambiguationData":[OSD([sQuery(id+"F8.wireOp",EDGE,"E26.bottom"),sQuery(id+"F8.wireOp",EDGE,"E26.right")])]})});
            var Q9;
            Q9=makeQuery(id+"F9.boolean.opBoolean","COPY",EDGE,{"derivedFrom":makeQuery(id+"F9.opExtrude","SWEPT_EDGE",EDGE,{"disambiguationData":[OSD([sQuery(id+"F8.wireOp",EDGE,"E26.top"),sQuery(id+"F8.wireOp",EDGE,"E26.right")])]})});
            var Q10;
            Q10=makeQuery(id+"F9.boolean.opBoolean","COPY",EDGE,{"derivedFrom":makeQuery(id+"F9.opExtrude","SWEPT_EDGE",EDGE,{"disambiguationData":[OSD([sQuery(id+"F8.wireOp",EDGE,"E32.MirrorCS"),sQuery(id+"F8.wireOp",EDGE,"E34.MirrorCS")])]})});
            var Q11;
            Q11=makeQuery(id+"F9.boolean.opBoolean","COPY",EDGE,{"derivedFrom":makeQuery(id+"F9.opExtrude","SWEPT_EDGE",EDGE,{"disambiguationData":[OSD([sQuery(id+"F8.wireOp",EDGE,"E33.MirrorCS"),sQuery(id+"F8.wireOp",EDGE,"E34.MirrorCS")])]})});
            var Q12;
            Q12=makeQuery(id+"F9.boolean.opBoolean","COPY",EDGE,{"derivedFrom":makeQuery(id+"F9.opExtrude","SWEPT_EDGE",EDGE,{"disambiguationData":[OSD([sQuery(id+"F8.wireOp",EDGE,"E28.MirrorCS"),sQuery(id+"F8.wireOp",EDGE,"E37.MirrorCS")])]})});
            var Q13;
            Q13=makeQuery(id+"F9.boolean.opBoolean","COPY",EDGE,{"derivedFrom":makeQuery(id+"F9.opExtrude","SWEPT_EDGE",EDGE,{"disambiguationData":[OSD([sQuery(id+"F8.wireOp",EDGE,"E37.MirrorCS"),sQuery(id+"F8.wireOp",EDGE,"E38.MirrorCS")])]})});
            var Q14;
            Q14=makeQuery(id+"F9.boolean.opBoolean","COPY",EDGE,{"derivedFrom":makeQuery(id+"F9.opExtrude","SWEPT_EDGE",EDGE,{"disambiguationData":[OSD([sQuery(id+"F8.wireOp",EDGE,"E31.MirrorCS"),sQuery(id+"F8.wireOp",EDGE,"E44.MirrorCS")])]})});
            var Q15;
            Q15=makeQuery(id+"F9.boolean.opBoolean","COPY",EDGE,{"derivedFrom":makeQuery(id+"F9.opExtrude","SWEPT_EDGE",EDGE,{"disambiguationData":[OSD([sQuery(id+"F8.wireOp",EDGE,"E30.MirrorCS"),sQuery(id+"F8.wireOp",EDGE,"E44.MirrorCS")])]})});
            var Q16;
            Q16=makeQuery(id+"F9.boolean.opBoolean","COPY",EDGE,{"derivedFrom":makeQuery(id+"F9.opExtrude","SWEPT_EDGE",EDGE,{"disambiguationData":[OSD([sQuery(id+"F8.wireOp",EDGE,"E41.MirrorCS"),sQuery(id+"F8.wireOp",EDGE,"E42.MirrorCS")])]})});
            var Q17;
            Q17=makeQuery(id+"F9.boolean.opBoolean","COPY",EDGE,{"derivedFrom":makeQuery(id+"F9.opExtrude","SWEPT_EDGE",EDGE,{"disambiguationData":[OSD([sQuery(id+"F8.wireOp",EDGE,"E40.MirrorCS"),sQuery(id+"F8.wireOp",EDGE,"E41.MirrorCS")])]})});
            var Q18;
            Q18=makeQuery(id+"F9.boolean.opBoolean","COPY",EDGE,{"derivedFrom":makeQuery(id+"F9.opExtrude","SWEPT_EDGE",EDGE,{"disambiguationData":[OSD([sQuery(id+"F8.wireOp",EDGE,"E29.MirrorCS"),sQuery(id+"F8.wireOp",EDGE,"E40.MirrorCS")])]})});
            var Q19;
            Q19=makeQuery(id+"F9.boolean.opBoolean","COPY",EDGE,{"derivedFrom":makeQuery(id+"F9.opExtrude","SWEPT_EDGE",EDGE,{"disambiguationData":[OSD([sQuery(id+"F8.wireOp",EDGE,"E29.MirrorCS"),sQuery(id+"F8.wireOp",EDGE,"E42.MirrorCS")])]})});
            var Q20;
            Q20=makeQuery(id+"F9.boolean.opBoolean","COPY",EDGE,{"derivedFrom":makeQuery(id+"F9.opExtrude","SWEPT_EDGE",EDGE,{"disambiguationData":[OSD([sQuery(id+"F8.wireOp",EDGE,"E30.MirrorCS"),sQuery(id+"F8.wireOp",EDGE,"E39.MirrorCS")])]})});
            var Q21;
            Q21=makeQuery(id+"F9.boolean.opBoolean","COPY",EDGE,{"derivedFrom":makeQuery(id+"F9.opExtrude","SWEPT_EDGE",EDGE,{"disambiguationData":[OSD([sQuery(id+"F8.wireOp",EDGE,"E31.MirrorCS"),sQuery(id+"F8.wireOp",EDGE,"E39.MirrorCS")])]})});
            var Q22;
            Q22=makeQuery(id+"F9.boolean.opBoolean","COPY",EDGE,{"derivedFrom":makeQuery(id+"F9.opExtrude","SWEPT_EDGE",EDGE,{"disambiguationData":[OSD([sQuery(id+"F8.wireOp",EDGE,"E28.MirrorCS"),sQuery(id+"F8.wireOp",EDGE,"E36.MirrorCS")])]})});
            var Q23;
            Q23=makeQuery(id+"F9.boolean.opBoolean","COPY",EDGE,{"derivedFrom":makeQuery(id+"F9.opExtrude","SWEPT_EDGE",EDGE,{"disambiguationData":[OSD([sQuery(id+"F8.wireOp",EDGE,"E36.MirrorCS"),sQuery(id+"F8.wireOp",EDGE,"E38.MirrorCS")])]})});
            var Q24;
            Q24=makeQuery(id+"F9.boolean.opBoolean","COPY",EDGE,{"derivedFrom":makeQuery(id+"F9.opExtrude","SWEPT_EDGE",EDGE,{"disambiguationData":[OSD([sQuery(id+"F8.wireOp",EDGE,"E32.MirrorCS"),sQuery(id+"F8.wireOp",EDGE,"E35.MirrorCS")])]})});
            var Q25;
            Q25=makeQuery(id+"F9.boolean.opBoolean","COPY",EDGE,{"derivedFrom":makeQuery(id+"F9.opExtrude","SWEPT_EDGE",EDGE,{"disambiguationData":[OSD([sQuery(id+"F8.wireOp",EDGE,"E33.MirrorCS"),sQuery(id+"F8.wireOp",EDGE,"E35.MirrorCS")])]})});
            var Q26;
            Q26=makeQuery(id+"F9.boolean.opBoolean","COPY",EDGE,{"derivedFrom":makeQuery(id+"F9.opExtrude","SWEPT_EDGE",EDGE,{"disambiguationData":[OSD([sQuery(id+"F8.wireOp",EDGE,"E26.top"),sQuery(id+"F8.wireOp",EDGE,"E26.left")])]})});
            var Q27;
            Q27=makeQuery(id+"F9.boolean.opBoolean","COPY",EDGE,{"derivedFrom":makeQuery(id+"F9.opExtrude","SWEPT_EDGE",EDGE,{"disambiguationData":[OSD([sQuery(id+"F8.wireOp",EDGE,"E26.bottom"),sQuery(id+"F8.wireOp",EDGE,"E26.left")])]})});
            var Q28;
            Q28=makeQuery(id+"F9.boolean.opBoolean","COPY",EDGE,{"derivedFrom":makeQuery(id+"F9.opExtrude","SWEPT_EDGE",EDGE,{"disambiguationData":[OSD([sQuery(id+"F8.wireOp",EDGE,"E27.1.0.1"),sQuery(id+"F8.wireOp",EDGE,"E27.1.0.3")])]})});
            var Q29;
            Q29=makeQuery(id+"F9.boolean.opBoolean","COPY",EDGE,{"derivedFrom":makeQuery(id+"F9.opExtrude","SWEPT_EDGE",EDGE,{"disambiguationData":[OSD([sQuery(id+"F8.wireOp",EDGE,"E27.1.0.1"),sQuery(id+"F8.wireOp",EDGE,"E27.1.0.2")])]})});
            var Q30;
            Q30=makeQuery(id+"F9.boolean.opBoolean","COPY",EDGE,{"derivedFrom":makeQuery(id+"F9.opExtrude","SWEPT_EDGE",EDGE,{"disambiguationData":[OSD([sQuery(id+"F8.wireOp",EDGE,"E27.2.0.1"),sQuery(id+"F8.wireOp",EDGE,"E27.2.0.2")])]})});
            var Q31;
            Q31=makeQuery(id+"F9.boolean.opBoolean","COPY",EDGE,{"derivedFrom":makeQuery(id+"F9.opExtrude","SWEPT_EDGE",EDGE,{"disambiguationData":[OSD([sQuery(id+"F8.wireOp",EDGE,"E27.2.0.1"),sQuery(id+"F8.wireOp",EDGE,"E27.2.0.3")])]})});
            fillet(context, id + "F10", {"entities" : qUnion([Q0, Q1, Q2, Q3, Q4, Q5, Q6, Q7, Q8, Q9, Q10, Q11, Q12, Q13, Q14, Q15, Q16, Q17, Q18, Q19, Q20, Q21, Q22, Q23, Q24, Q25, Q26, Q27, Q28, Q29, Q30, Q31]), "radius" : 1.59 * mm, "tangentPropagation" : true, "allowEdgeOverflow" : false});
        }
        {
            var Q0;
            Q0=makeQuery(id+"F7.boolean.opBoolean","COPY",EDGE,{"derivedFrom":makeQuery(id+"F7.opExtrude","SWEPT_EDGE",EDGE,{"disambiguationData":[OSD([sQuery(id+"F6.wireOp",EDGE,"E14.left"),sQuery(id+"F6.wireOp",EDGE,"E16")])]})});
            var Q1;
            Q1=makeQuery(id+"F7.boolean.opBoolean","COPY",EDGE,{"derivedFrom":makeQuery(id+"F7.opExtrude","SWEPT_EDGE",EDGE,{"disambiguationData":[OSD([sQuery(id+"F6.wireOp",EDGE,"E14.top"),sQuery(id+"F6.wireOp",EDGE,"E20.trimOffspring")])]})});
            var Q2;
            Q2=makeQuery(id+"F7.boolean.opBoolean","COPY",EDGE,{"derivedFrom":makeQuery(id+"F7.opExtrude","SWEPT_EDGE",EDGE,{"disambiguationData":[OSD([sQuery(id+"F6.wireOp",EDGE,"E14.left"),sQuery(id+"F6.wireOp",EDGE,"E15")])]})});
            var Q3;
            Q3=makeQuery(id+"F7.boolean.opBoolean","COPY",EDGE,{"derivedFrom":makeQuery(id+"F7.opExtrude","SWEPT_EDGE",EDGE,{"disambiguationData":[OSD([sQuery(id+"F6.wireOp",EDGE,"E17"),sQuery(id+"F6.wireOp",EDGE,"E19.trimOffspring")])]})});
            var Q4;
            Q4=makeQuery(id+"F7.boolean.opBoolean","COPY",EDGE,{"derivedFrom":makeQuery(id+"F7.opExtrude","SWEPT_EDGE",EDGE,{"disambiguationData":[OSD([sQuery(id+"F6.wireOp",EDGE,"E18"),sQuery(id+"F6.wireOp",EDGE,"E19.trimOffspring")])]})});
            var Q5;
            Q5=makeQuery(id+"F7.boolean.opBoolean","COPY",EDGE,{"derivedFrom":makeQuery(id+"F7.opExtrude","SWEPT_EDGE",EDGE,{"disambiguationData":[OSD([sQuery(id+"F6.wireOp",EDGE,"E14.right"),sQuery(id+"F6.wireOp",EDGE,"E21.trimOffspring")])]})});
            var Q6;
            Q6=makeQuery(id+"F7.boolean.opBoolean","COPY",EDGE,{"derivedFrom":makeQuery(id+"F7.opExtrude","SWEPT_EDGE",EDGE,{"disambiguationData":[OSD([sQuery(id+"F6.wireOp",EDGE,"E14.right"),sQuery(id+"F6.wireOp",EDGE,"E23.trimOffspring")])]})});
            var Q7;
            Q7=makeQuery(id+"F7.boolean.opBoolean","COPY",EDGE,{"derivedFrom":makeQuery(id+"F7.opExtrude","SWEPT_EDGE",EDGE,{"disambiguationData":[OSD([sQuery(id+"F6.wireOp",EDGE,"E14.top"),sQuery(id+"F6.wireOp",EDGE,"E22.trimOffspring")])]})});
            var Q8;
            Q8=makeQuery(id+"F7.boolean.opBoolean","COPY",EDGE,{"derivedFrom":makeQuery(id+"F7.opExtrude","SWEPT_EDGE",EDGE,{"disambiguationData":[OSD([sQuery(id+"F6.wireOp",EDGE,"E25.1.0.10"),sQuery(id+"F6.wireOp",EDGE,"E25.1.0.14")])]})});
            var Q9;
            Q9=makeQuery(id+"F7.boolean.opBoolean","COPY",EDGE,{"derivedFrom":makeQuery(id+"F7.opExtrude","SWEPT_EDGE",EDGE,{"disambiguationData":[OSD([sQuery(id+"F6.wireOp",EDGE,"E25.1.0.11"),sQuery(id+"F6.wireOp",EDGE,"E25.1.0.17")])]})});
            var Q10;
            Q10=makeQuery(id+"F7.boolean.opBoolean","COPY",EDGE,{"derivedFrom":makeQuery(id+"F7.opExtrude","SWEPT_EDGE",EDGE,{"disambiguationData":[OSD([sQuery(id+"F6.wireOp",EDGE,"E25.1.0.11"),sQuery(id+"F6.wireOp",EDGE,"E25.1.0.23")])]})});
            var Q11;
            Q11=makeQuery(id+"F7.boolean.opBoolean","COPY",EDGE,{"derivedFrom":makeQuery(id+"F7.opExtrude","SWEPT_EDGE",EDGE,{"disambiguationData":[OSD([sQuery(id+"F6.wireOp",EDGE,"E25.1.0.9"),sQuery(id+"F6.wireOp",EDGE,"E25.1.0.15")])]})});
            var Q12;
            Q12=makeQuery(id+"F7.boolean.opBoolean","COPY",EDGE,{"derivedFrom":makeQuery(id+"F7.opExtrude","SWEPT_EDGE",EDGE,{"disambiguationData":[OSD([sQuery(id+"F6.wireOp",EDGE,"E25.1.0.9"),sQuery(id+"F6.wireOp",EDGE,"E25.1.0.18")])]})});
            var Q13;
            Q13=makeQuery(id+"F7.boolean.opBoolean","COPY",EDGE,{"derivedFrom":makeQuery(id+"F7.opExtrude","SWEPT_EDGE",EDGE,{"disambiguationData":[OSD([sQuery(id+"F6.wireOp",EDGE,"E25.1.0.8"),sQuery(id+"F6.wireOp",EDGE,"E25.1.0.25")])]})});
            var Q14;
            Q14=makeQuery(id+"F7.boolean.opBoolean","COPY",EDGE,{"derivedFrom":makeQuery(id+"F7.opExtrude","SWEPT_EDGE",EDGE,{"disambiguationData":[OSD([sQuery(id+"F6.wireOp",EDGE,"E25.1.0.10"),sQuery(id+"F6.wireOp",EDGE,"E25.1.0.22")])]})});
            var Q15;
            Q15=makeQuery(id+"F7.boolean.opBoolean","COPY",EDGE,{"derivedFrom":makeQuery(id+"F7.opExtrude","SWEPT_EDGE",EDGE,{"disambiguationData":[OSD([sQuery(id+"F6.wireOp",EDGE,"E25.1.0.8"),sQuery(id+"F6.wireOp",EDGE,"E25.1.0.27")])]})});
            var Q16;
            Q16=makeQuery(id+"F7.boolean.opBoolean","COPY",EDGE,{"derivedFrom":makeQuery(id+"F7.opExtrude","SWEPT_EDGE",EDGE,{"disambiguationData":[OSD([sQuery(id+"F6.wireOp",EDGE,"E25.2.0.10"),sQuery(id+"F6.wireOp",EDGE,"E25.2.0.22")])]})});
            var Q17;
            Q17=makeQuery(id+"F7.boolean.opBoolean","COPY",EDGE,{"derivedFrom":makeQuery(id+"F7.opExtrude","SWEPT_EDGE",EDGE,{"disambiguationData":[OSD([sQuery(id+"F6.wireOp",EDGE,"E25.2.0.8"),sQuery(id+"F6.wireOp",EDGE,"E25.2.0.27")])]})});
            var Q18;
            Q18=makeQuery(id+"F7.boolean.opBoolean","COPY",EDGE,{"derivedFrom":makeQuery(id+"F7.opExtrude","SWEPT_EDGE",EDGE,{"disambiguationData":[OSD([sQuery(id+"F6.wireOp",EDGE,"E25.2.0.10"),sQuery(id+"F6.wireOp",EDGE,"E25.2.0.14")])]})});
            var Q19;
            Q19=makeQuery(id+"F7.boolean.opBoolean","COPY",EDGE,{"derivedFrom":makeQuery(id+"F7.opExtrude","SWEPT_EDGE",EDGE,{"disambiguationData":[OSD([sQuery(id+"F6.wireOp",EDGE,"E25.2.0.11"),sQuery(id+"F6.wireOp",EDGE,"E25.2.0.17")])]})});
            var Q20;
            Q20=makeQuery(id+"F7.boolean.opBoolean","COPY",EDGE,{"derivedFrom":makeQuery(id+"F7.opExtrude","SWEPT_EDGE",EDGE,{"disambiguationData":[OSD([sQuery(id+"F6.wireOp",EDGE,"E25.2.0.9"),sQuery(id+"F6.wireOp",EDGE,"E25.2.0.15")])]})});
            var Q21;
            Q21=makeQuery(id+"F7.boolean.opBoolean","COPY",EDGE,{"derivedFrom":makeQuery(id+"F7.opExtrude","SWEPT_EDGE",EDGE,{"disambiguationData":[OSD([sQuery(id+"F6.wireOp",EDGE,"E25.2.0.11"),sQuery(id+"F6.wireOp",EDGE,"E25.2.0.23")])]})});
            var Q22;
            Q22=makeQuery(id+"F7.boolean.opBoolean","COPY",EDGE,{"derivedFrom":makeQuery(id+"F7.opExtrude","SWEPT_EDGE",EDGE,{"disambiguationData":[OSD([sQuery(id+"F6.wireOp",EDGE,"E25.2.0.8"),sQuery(id+"F6.wireOp",EDGE,"E25.2.0.25")])]})});
            var Q23;
            Q23=makeQuery(id+"F7.boolean.opBoolean","COPY",EDGE,{"derivedFrom":makeQuery(id+"F7.opExtrude","SWEPT_EDGE",EDGE,{"disambiguationData":[OSD([sQuery(id+"F6.wireOp",EDGE,"E25.2.0.9"),sQuery(id+"F6.wireOp",EDGE,"E25.2.0.18")])]})});
            var Q24;
            Q24=makeQuery(id+"F7.boolean.opBoolean","COPY",EDGE,{"derivedFrom":makeQuery(id+"F7.opExtrude","SWEPT_EDGE",EDGE,{"disambiguationData":[OSD([sQuery(id+"F6.wireOp",EDGE,"E25.3.0.9"),sQuery(id+"F6.wireOp",EDGE,"E25.3.0.18")])]})});
            var Q25;
            Q25=makeQuery(id+"F7.boolean.opBoolean","COPY",EDGE,{"derivedFrom":makeQuery(id+"F7.opExtrude","SWEPT_EDGE",EDGE,{"disambiguationData":[OSD([sQuery(id+"F6.wireOp",EDGE,"E25.3.0.8"),sQuery(id+"F6.wireOp",EDGE,"E25.3.0.25")])]})});
            var Q26;
            Q26=makeQuery(id+"F7.boolean.opBoolean","COPY",EDGE,{"derivedFrom":makeQuery(id+"F7.opExtrude","SWEPT_EDGE",EDGE,{"disambiguationData":[OSD([sQuery(id+"F6.wireOp",EDGE,"E25.3.0.11"),sQuery(id+"F6.wireOp",EDGE,"E25.3.0.23")])]})});
            var Q27;
            Q27=makeQuery(id+"F7.boolean.opBoolean","COPY",EDGE,{"derivedFrom":makeQuery(id+"F7.opExtrude","SWEPT_EDGE",EDGE,{"disambiguationData":[OSD([sQuery(id+"F6.wireOp",EDGE,"E25.3.0.9"),sQuery(id+"F6.wireOp",EDGE,"E25.3.0.15")])]})});
            var Q28;
            Q28=makeQuery(id+"F7.boolean.opBoolean","COPY",EDGE,{"derivedFrom":makeQuery(id+"F7.opExtrude","SWEPT_EDGE",EDGE,{"disambiguationData":[OSD([sQuery(id+"F6.wireOp",EDGE,"E25.3.0.10"),sQuery(id+"F6.wireOp",EDGE,"E25.3.0.14")])]})});
            var Q29;
            Q29=makeQuery(id+"F7.boolean.opBoolean","COPY",EDGE,{"derivedFrom":makeQuery(id+"F7.opExtrude","SWEPT_EDGE",EDGE,{"disambiguationData":[OSD([sQuery(id+"F6.wireOp",EDGE,"E25.3.0.11"),sQuery(id+"F6.wireOp",EDGE,"E25.3.0.17")])]})});
            var Q30;
            Q30=makeQuery(id+"F7.boolean.opBoolean","COPY",EDGE,{"derivedFrom":makeQuery(id+"F7.opExtrude","SWEPT_EDGE",EDGE,{"disambiguationData":[OSD([sQuery(id+"F6.wireOp",EDGE,"E25.3.0.10"),sQuery(id+"F6.wireOp",EDGE,"E25.3.0.22")])]})});
            var Q31;
            Q31=makeQuery(id+"F7.boolean.opBoolean","COPY",EDGE,{"derivedFrom":makeQuery(id+"F7.opExtrude","SWEPT_EDGE",EDGE,{"disambiguationData":[OSD([sQuery(id+"F6.wireOp",EDGE,"E25.3.0.8"),sQuery(id+"F6.wireOp",EDGE,"E25.3.0.27")])]})});
            var Q32;
            Q32=makeQuery(id+"F7.boolean.opBoolean","COPY",EDGE,{"derivedFrom":makeQuery(id+"F7.opExtrude","SWEPT_EDGE",EDGE,{"disambiguationData":[OSD([sQuery(id+"F6.wireOp",EDGE,"E25.4.0.10"),sQuery(id+"F6.wireOp",EDGE,"E25.4.0.14")])]})});
            var Q33;
            Q33=makeQuery(id+"F7.boolean.opBoolean","COPY",EDGE,{"derivedFrom":makeQuery(id+"F7.opExtrude","SWEPT_EDGE",EDGE,{"disambiguationData":[OSD([sQuery(id+"F6.wireOp",EDGE,"E25.4.0.11"),sQuery(id+"F6.wireOp",EDGE,"E25.4.0.17")])]})});
            var Q34;
            Q34=makeQuery(id+"F7.boolean.opBoolean","COPY",EDGE,{"derivedFrom":makeQuery(id+"F7.opExtrude","SWEPT_EDGE",EDGE,{"disambiguationData":[OSD([sQuery(id+"F6.wireOp",EDGE,"E25.4.0.11"),sQuery(id+"F6.wireOp",EDGE,"E25.4.0.23")])]})});
            var Q35;
            Q35=makeQuery(id+"F7.boolean.opBoolean","COPY",EDGE,{"derivedFrom":makeQuery(id+"F7.opExtrude","SWEPT_EDGE",EDGE,{"disambiguationData":[OSD([sQuery(id+"F6.wireOp",EDGE,"E25.4.0.9"),sQuery(id+"F6.wireOp",EDGE,"E25.4.0.15")])]})});
            var Q36;
            Q36=makeQuery(id+"F7.boolean.opBoolean","COPY",EDGE,{"derivedFrom":makeQuery(id+"F7.opExtrude","SWEPT_EDGE",EDGE,{"disambiguationData":[OSD([sQuery(id+"F6.wireOp",EDGE,"E25.4.0.9"),sQuery(id+"F6.wireOp",EDGE,"E25.4.0.18")])]})});
            var Q37;
            Q37=makeQuery(id+"F7.boolean.opBoolean","COPY",EDGE,{"derivedFrom":makeQuery(id+"F7.opExtrude","SWEPT_EDGE",EDGE,{"disambiguationData":[OSD([sQuery(id+"F6.wireOp",EDGE,"E25.4.0.8"),sQuery(id+"F6.wireOp",EDGE,"E25.4.0.25")])]})});
            var Q38;
            Q38=makeQuery(id+"F7.boolean.opBoolean","COPY",EDGE,{"derivedFrom":makeQuery(id+"F7.opExtrude","SWEPT_EDGE",EDGE,{"disambiguationData":[OSD([sQuery(id+"F6.wireOp",EDGE,"E25.4.0.8"),sQuery(id+"F6.wireOp",EDGE,"E25.4.0.27")])]})});
            var Q39;
            Q39=makeQuery(id+"F7.boolean.opBoolean","COPY",EDGE,{"derivedFrom":makeQuery(id+"F7.opExtrude","SWEPT_EDGE",EDGE,{"disambiguationData":[OSD([sQuery(id+"F6.wireOp",EDGE,"E25.4.0.10"),sQuery(id+"F6.wireOp",EDGE,"E25.4.0.22")])]})});
            var Q40;
            Q40=makeQuery(id+"F7.boolean.opBoolean","COPY",EDGE,{"derivedFrom":makeQuery(id+"F7.opExtrude","SWEPT_EDGE",EDGE,{"disambiguationData":[OSD([sQuery(id+"F6.wireOp",EDGE,"E25.5.0.10"),sQuery(id+"F6.wireOp",EDGE,"E25.5.0.14")])]})});
            var Q41;
            Q41=makeQuery(id+"F7.boolean.opBoolean","COPY",EDGE,{"derivedFrom":makeQuery(id+"F7.opExtrude","SWEPT_EDGE",EDGE,{"disambiguationData":[OSD([sQuery(id+"F6.wireOp",EDGE,"E25.5.0.11"),sQuery(id+"F6.wireOp",EDGE,"E25.5.0.17")])]})});
            var Q42;
            Q42=makeQuery(id+"F7.boolean.opBoolean","COPY",EDGE,{"derivedFrom":makeQuery(id+"F7.opExtrude","SWEPT_EDGE",EDGE,{"disambiguationData":[OSD([sQuery(id+"F6.wireOp",EDGE,"E25.5.0.11"),sQuery(id+"F6.wireOp",EDGE,"E25.5.0.23")])]})});
            var Q43;
            Q43=makeQuery(id+"F7.boolean.opBoolean","COPY",EDGE,{"derivedFrom":makeQuery(id+"F7.opExtrude","SWEPT_EDGE",EDGE,{"disambiguationData":[OSD([sQuery(id+"F6.wireOp",EDGE,"E25.5.0.9"),sQuery(id+"F6.wireOp",EDGE,"E25.5.0.15")])]})});
            var Q44;
            Q44=makeQuery(id+"F7.boolean.opBoolean","COPY",EDGE,{"derivedFrom":makeQuery(id+"F7.opExtrude","SWEPT_EDGE",EDGE,{"disambiguationData":[OSD([sQuery(id+"F6.wireOp",EDGE,"E25.5.0.9"),sQuery(id+"F6.wireOp",EDGE,"E25.5.0.18")])]})});
            var Q45;
            Q45=makeQuery(id+"F7.boolean.opBoolean","COPY",EDGE,{"derivedFrom":makeQuery(id+"F7.opExtrude","SWEPT_EDGE",EDGE,{"disambiguationData":[OSD([sQuery(id+"F6.wireOp",EDGE,"E25.5.0.8"),sQuery(id+"F6.wireOp",EDGE,"E25.5.0.25")])]})});
            var Q46;
            Q46=makeQuery(id+"F7.boolean.opBoolean","COPY",EDGE,{"derivedFrom":makeQuery(id+"F7.opExtrude","SWEPT_EDGE",EDGE,{"disambiguationData":[OSD([sQuery(id+"F6.wireOp",EDGE,"E25.5.0.8"),sQuery(id+"F6.wireOp",EDGE,"E25.5.0.27")])]})});
            var Q47;
            Q47=makeQuery(id+"F7.boolean.opBoolean","COPY",EDGE,{"derivedFrom":makeQuery(id+"F7.opExtrude","SWEPT_EDGE",EDGE,{"disambiguationData":[OSD([sQuery(id+"F6.wireOp",EDGE,"E25.5.0.10"),sQuery(id+"F6.wireOp",EDGE,"E25.5.0.22")])]})});
            var Q48;
            Q48=makeQuery(id+"F7.boolean.opBoolean","COPY",EDGE,{"derivedFrom":makeQuery(id+"F7.opExtrude","SWEPT_EDGE",EDGE,{"disambiguationData":[OSD([sQuery(id+"F6.wireOp",EDGE,"E25.6.0.10"),sQuery(id+"F6.wireOp",EDGE,"E25.6.0.22")])]})});
            var Q49;
            Q49=makeQuery(id+"F7.boolean.opBoolean","COPY",EDGE,{"derivedFrom":makeQuery(id+"F7.opExtrude","SWEPT_EDGE",EDGE,{"disambiguationData":[OSD([sQuery(id+"F6.wireOp",EDGE,"E25.6.0.8"),sQuery(id+"F6.wireOp",EDGE,"E25.6.0.27")])]})});
            var Q50;
            Q50=makeQuery(id+"F7.boolean.opBoolean","COPY",EDGE,{"derivedFrom":makeQuery(id+"F7.opExtrude","SWEPT_EDGE",EDGE,{"disambiguationData":[OSD([sQuery(id+"F6.wireOp",EDGE,"E25.6.0.8"),sQuery(id+"F6.wireOp",EDGE,"E25.6.0.25")])]})});
            var Q51;
            Q51=makeQuery(id+"F7.boolean.opBoolean","COPY",EDGE,{"derivedFrom":makeQuery(id+"F7.opExtrude","SWEPT_EDGE",EDGE,{"disambiguationData":[OSD([sQuery(id+"F6.wireOp",EDGE,"E25.6.0.9"),sQuery(id+"F6.wireOp",EDGE,"E25.6.0.18")])]})});
            var Q52;
            Q52=makeQuery(id+"F7.boolean.opBoolean","COPY",EDGE,{"derivedFrom":makeQuery(id+"F7.opExtrude","SWEPT_EDGE",EDGE,{"disambiguationData":[OSD([sQuery(id+"F6.wireOp",EDGE,"E25.6.0.11"),sQuery(id+"F6.wireOp",EDGE,"E25.6.0.23")])]})});
            var Q53;
            Q53=makeQuery(id+"F7.boolean.opBoolean","COPY",EDGE,{"derivedFrom":makeQuery(id+"F7.opExtrude","SWEPT_EDGE",EDGE,{"disambiguationData":[OSD([sQuery(id+"F6.wireOp",EDGE,"E25.6.0.9"),sQuery(id+"F6.wireOp",EDGE,"E25.6.0.15")])]})});
            var Q54;
            Q54=makeQuery(id+"F7.boolean.opBoolean","COPY",EDGE,{"derivedFrom":makeQuery(id+"F7.opExtrude","SWEPT_EDGE",EDGE,{"disambiguationData":[OSD([sQuery(id+"F6.wireOp",EDGE,"E25.6.0.10"),sQuery(id+"F6.wireOp",EDGE,"E25.6.0.14")])]})});
            var Q55;
            Q55=makeQuery(id+"F7.boolean.opBoolean","COPY",EDGE,{"derivedFrom":makeQuery(id+"F7.opExtrude","SWEPT_EDGE",EDGE,{"disambiguationData":[OSD([sQuery(id+"F6.wireOp",EDGE,"E25.6.0.11"),sQuery(id+"F6.wireOp",EDGE,"E25.6.0.17")])]})});
            var Q56;
            Q56=makeQuery(id+"F7.boolean.opBoolean","COPY",EDGE,{"derivedFrom":makeQuery(id+"F7.opExtrude","SWEPT_EDGE",EDGE,{"disambiguationData":[OSD([sQuery(id+"F6.wireOp",EDGE,"E25.7.0.11"),sQuery(id+"F6.wireOp",EDGE,"E25.7.0.17")])]})});
            var Q57;
            Q57=makeQuery(id+"F7.boolean.opBoolean","COPY",EDGE,{"derivedFrom":makeQuery(id+"F7.opExtrude","SWEPT_EDGE",EDGE,{"disambiguationData":[OSD([sQuery(id+"F6.wireOp",EDGE,"E25.7.0.10"),sQuery(id+"F6.wireOp",EDGE,"E25.7.0.14")])]})});
            var Q58;
            Q58=makeQuery(id+"F7.boolean.opBoolean","COPY",EDGE,{"derivedFrom":makeQuery(id+"F7.opExtrude","SWEPT_EDGE",EDGE,{"disambiguationData":[OSD([sQuery(id+"F6.wireOp",EDGE,"E25.7.0.10"),sQuery(id+"F6.wireOp",EDGE,"E25.7.0.22")])]})});
            var Q59;
            Q59=makeQuery(id+"F7.boolean.opBoolean","COPY",EDGE,{"derivedFrom":makeQuery(id+"F7.opExtrude","SWEPT_EDGE",EDGE,{"disambiguationData":[OSD([sQuery(id+"F6.wireOp",EDGE,"E25.7.0.8"),sQuery(id+"F6.wireOp",EDGE,"E25.7.0.27")])]})});
            var Q60;
            Q60=makeQuery(id+"F7.boolean.opBoolean","COPY",EDGE,{"derivedFrom":makeQuery(id+"F7.opExtrude","SWEPT_EDGE",EDGE,{"disambiguationData":[OSD([sQuery(id+"F6.wireOp",EDGE,"E25.7.0.11"),sQuery(id+"F6.wireOp",EDGE,"E25.7.0.23")])]})});
            var Q61;
            Q61=makeQuery(id+"F7.boolean.opBoolean","COPY",EDGE,{"derivedFrom":makeQuery(id+"F7.opExtrude","SWEPT_EDGE",EDGE,{"disambiguationData":[OSD([sQuery(id+"F6.wireOp",EDGE,"E25.7.0.9"),sQuery(id+"F6.wireOp",EDGE,"E25.7.0.15")])]})});
            var Q62;
            Q62=makeQuery(id+"F7.boolean.opBoolean","COPY",EDGE,{"derivedFrom":makeQuery(id+"F7.opExtrude","SWEPT_EDGE",EDGE,{"disambiguationData":[OSD([sQuery(id+"F6.wireOp",EDGE,"E25.7.0.8"),sQuery(id+"F6.wireOp",EDGE,"E25.7.0.25")])]})});
            var Q63;
            Q63=makeQuery(id+"F7.boolean.opBoolean","COPY",EDGE,{"derivedFrom":makeQuery(id+"F7.opExtrude","SWEPT_EDGE",EDGE,{"disambiguationData":[OSD([sQuery(id+"F6.wireOp",EDGE,"E25.7.0.9"),sQuery(id+"F6.wireOp",EDGE,"E25.7.0.18")])]})});
            fillet(context, id + "F11", {"entities" : qUnion([Q0, Q1, Q2, Q3, Q4, Q5, Q6, Q7, Q8, Q9, Q10, Q11, Q12, Q13, Q14, Q15, Q16, Q17, Q18, Q19, Q20, Q21, Q22, Q23, Q24, Q25, Q26, Q27, Q28, Q29, Q30, Q31, Q32, Q33, Q34, Q35, Q36, Q37, Q38, Q39, Q40, Q41, Q42, Q43, Q44, Q45, Q46, Q47, Q48, Q49, Q50, Q51, Q52, Q53, Q54, Q55, Q56, Q57, Q58, Q59, Q60, Q61, Q62, Q63]), "radius" : 1.59 * mm, "tangentPropagation" : true, "allowEdgeOverflow" : false});
        }
    });
